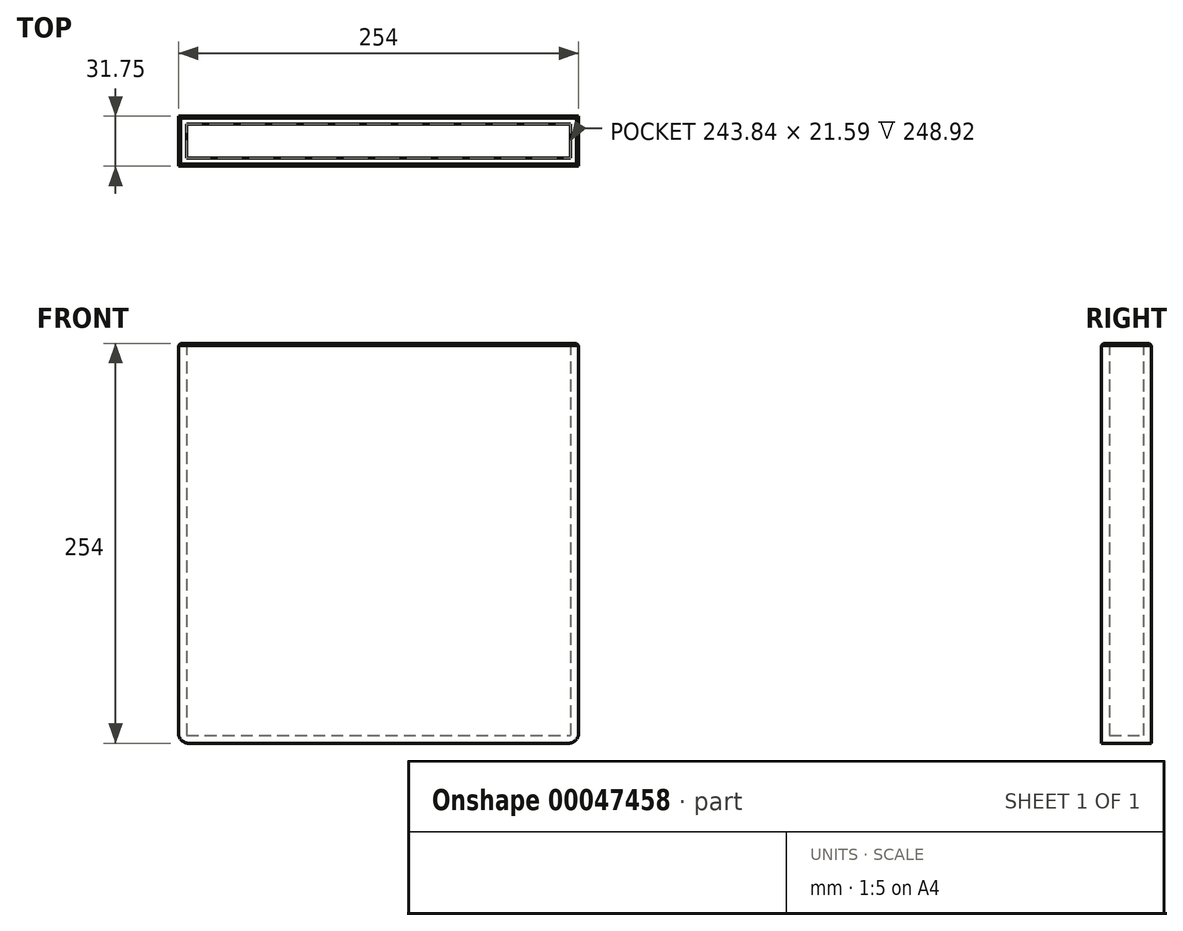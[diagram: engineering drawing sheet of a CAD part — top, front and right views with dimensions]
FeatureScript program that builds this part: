
annotation { "Feature Type Name" : "Feature", "Feature Type Description" : "" }
export const myFeature = defineFeature(function(context is Context, id is Id, definition is map)
    precondition{}
    {
        {
            var Q0;
            Q0=qCreatedBy(makeId("Front.planeOp"),FACE);
            var sketch = newSketch(context, id + "F0", { "sketchPlane" : qUnion([Q0])});
            skLineSegment(sketch, "E0.bottom", {"start": v(-124.91, 138.79) * mm, "end": v(129.09, 138.79) * mm});
            skLineSegment(sketch, "E0.top", {"start": v(-124.91, -115.21) * mm, "end": v(129.09, -115.21) * mm});
            skLineSegment(sketch, "E0.left", {"start": v(-124.91, 138.79) * mm, "end": v(-124.91, -115.21) * mm});
            skLineSegment(sketch, "E0.right", {"start": v(129.09, 138.79) * mm, "end": v(129.09, -115.21) * mm});
            skSolve(sketch);
        }
        {
            var Q0;
            Q0=makeQuery(id+"F0.imprint","IMPRINT",FACE,{"disambiguationData":[TD([[makeQuery(id+"F0.imprint","IMPRINT",EDGE,{"derivedFrom":sQuery(id+"F0.wireOp",EDGE,"E0.bottom")}),-1.0]])]});
            extrude(context, id + "F1", {"entities" : qUnion([Q0]), "depth" : 31.75 * mm});
        }
        {
            var Q0;
            Q0=makeQuery(id+"F1.opExtrude","SWEPT_FACE",FACE,{"disambiguationData":[OSD([sQuery(id+"F0.wireOp",EDGE,"E0.bottom")])]});
            shell(context, id + "F2", {"entities" : qUnion([Q0]), "thickness" : 5.08 * mm});
        }
        {
            var Q0;
            Q0=makeQuery(id+"F1.opExtrude","CAP_EDGE",EDGE,{"disambiguationData":[OSD([sQuery(id+"F0.wireOp",EDGE,"E0.bottom")])],"isStart":false});
            var Q1;
            Q1=makeQuery(id+"F1.opExtrude","SWEPT_EDGE",EDGE,{"disambiguationData":[OSD([sQuery(id+"F0.wireOp",EDGE,"E0.bottom"),sQuery(id+"F0.wireOp",EDGE,"E0.left")])]});
            var Q2;
            Q2=makeQuery(id+"F1.opExtrude","CAP_EDGE",EDGE,{"disambiguationData":[OSD([sQuery(id+"F0.wireOp",EDGE,"E0.bottom")])],"isStart":true});
            var Q3;
            Q3=makeQuery(id+"F1.opExtrude","SWEPT_EDGE",EDGE,{"disambiguationData":[OSD([sQuery(id+"F0.wireOp",EDGE,"E0.bottom"),sQuery(id+"F0.wireOp",EDGE,"E0.right")])]});
            chamfer(context, id + "F3", {"entities" : qUnion([Q0, Q1, Q2, Q3]), "width" : 1.27 * mm, "tangentPropagation" : true});
        }
        {
            var Q0;
            Q0=makeQuery(id+"F1.opExtrude","SWEPT_EDGE",EDGE,{"disambiguationData":[OSD([sQuery(id+"F0.wireOp",EDGE,"E0.top"),sQuery(id+"F0.wireOp",EDGE,"E0.right")])]});
            var Q1;
            Q1=makeQuery(id+"F1.opExtrude","SWEPT_EDGE",EDGE,{"disambiguationData":[OSD([sQuery(id+"F0.wireOp",EDGE,"E0.top"),sQuery(id+"F0.wireOp",EDGE,"E0.left")])]});
            fillet(context, id + "F4", {"entities" : qUnion([Q0, Q1]), "radius" : 6.35 * mm, "tangentPropagation" : true, "allowEdgeOverflow" : false});
        }
    });
